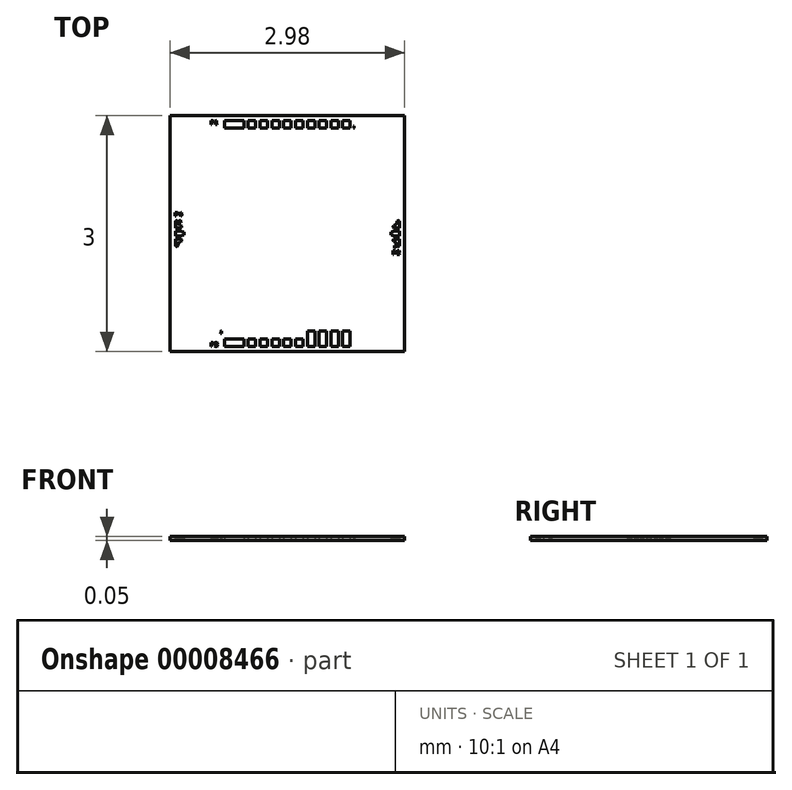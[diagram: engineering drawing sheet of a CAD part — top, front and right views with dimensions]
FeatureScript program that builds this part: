
annotation { "Feature Type Name" : "Feature", "Feature Type Description" : "" }
export const myFeature = defineFeature(function(context is Context, id is Id, definition is map)
    precondition{}
    {
        {
            var Q0;
            Q0=qCreatedBy(makeId("Top.planeOp"),FACE);
            var sketch = newSketch(context, id + "F0", { "sketchPlane" : qUnion([Q0])});
            skLineSegment(sketch, "E0", {"start": v(-1.43, 0.22) * mm, "end": v(-1.43, 0.27) * mm});
            skLineSegment(sketch, "E1", {"start": v(-1.43, 0.27) * mm, "end": v(-1.4, 0.27) * mm});
            skLineSegment(sketch, "E2", {"start": v(-1.4, 0.27) * mm, "end": v(-1.39, 0.26) * mm});
            skLineSegment(sketch, "E3", {"start": v(-1.39, 0.26) * mm, "end": v(-1.39, 0.25) * mm});
            skLineSegment(sketch, "E4", {"start": v(-1.39, 0.25) * mm, "end": v(-1.4, 0.24) * mm});
            skLineSegment(sketch, "E5", {"start": v(-1.4, 0.24) * mm, "end": v(-1.42, 0.24) * mm});
            skLineSegment(sketch, "E6", {"start": v(-1.42, 0.24) * mm, "end": v(-1.42, 0.22) * mm});
            skLineSegment(sketch, "E7", {"start": v(-1.42, 0.22) * mm, "end": v(-1.43, 0.22) * mm});
            skLineSegment(sketch, "E8", {"start": v(-1.42, -0.15) * mm, "end": v(-1.42, -0.07) * mm});
            skLineSegment(sketch, "E9", {"start": v(-1.42, -0.07) * mm, "end": v(-1.36, -0.07) * mm});
            skLineSegment(sketch, "E10", {"start": v(-1.36, -0.07) * mm, "end": v(-1.35, -0.07) * mm});
            skLineSegment(sketch, "E11", {"start": v(-1.35, -0.07) * mm, "end": v(-1.35, -0.07) * mm});
            skLineSegment(sketch, "E12", {"start": v(-1.35, -0.07) * mm, "end": v(-1.35, -0.08) * mm});
            skLineSegment(sketch, "E13", {"start": v(-1.35, -0.08) * mm, "end": v(-1.34, -0.08) * mm});
            skLineSegment(sketch, "E14", {"start": v(-1.34, -0.08) * mm, "end": v(-1.34, -0.09) * mm});
            skLineSegment(sketch, "E15", {"start": v(-1.34, -0.09) * mm, "end": v(-1.34, -0.1) * mm});
            skLineSegment(sketch, "E16", {"start": v(-1.34, -0.1) * mm, "end": v(-1.35, -0.1) * mm});
            skLineSegment(sketch, "E17", {"start": v(-1.35, -0.1) * mm, "end": v(-1.35, -0.1) * mm});
            skLineSegment(sketch, "E18", {"start": v(-1.35, -0.1) * mm, "end": v(-1.36, -0.1) * mm});
            skLineSegment(sketch, "E19", {"start": v(-1.36, -0.1) * mm, "end": v(-1.37, -0.1) * mm});
            skLineSegment(sketch, "E20", {"start": v(-1.37, -0.1) * mm, "end": v(-1.4, -0.14) * mm});
            skLineSegment(sketch, "E21", {"start": v(-1.4, -0.14) * mm, "end": v(-1.4, -0.15) * mm});
            skLineSegment(sketch, "E22", {"start": v(-1.4, -0.15) * mm, "end": v(-1.4, -0.15) * mm});
            skLineSegment(sketch, "E23", {"start": v(-1.4, -0.15) * mm, "end": v(-1.4, -0.16) * mm});
            skLineSegment(sketch, "E24", {"start": v(-1.4, -0.16) * mm, "end": v(-1.4, -0.16) * mm});
            skLineSegment(sketch, "E25", {"start": v(-1.4, -0.16) * mm, "end": v(-1.41, -0.16) * mm});
            skLineSegment(sketch, "E26", {"start": v(-1.41, -0.16) * mm, "end": v(-1.42, -0.16) * mm});
            skLineSegment(sketch, "E27", {"start": v(-1.42, -0.16) * mm, "end": v(-1.42, -0.16) * mm});
            skLineSegment(sketch, "E28", {"start": v(-1.42, -0.16) * mm, "end": v(-1.42, -0.15) * mm});
            skLineSegment(sketch, "E29", {"start": v(-1.42, -0.15) * mm, "end": v(-1.42, -0.15) * mm});
            skLineSegment(sketch, "E30", {"start": v(-1.42, -0.03) * mm, "end": v(-1.42, 0.03) * mm});
            skLineSegment(sketch, "E31", {"start": v(-1.42, 0.03) * mm, "end": v(-1.36, 0.03) * mm});
            skLineSegment(sketch, "E32", {"start": v(-1.36, 0.03) * mm, "end": v(-1.33, 0.02) * mm});
            skLineSegment(sketch, "E33", {"start": v(-1.33, 0.02) * mm, "end": v(-1.32, 0.02) * mm});
            skLineSegment(sketch, "E34", {"start": v(-1.32, 0.02) * mm, "end": v(-1.32, -0.02) * mm});
            skLineSegment(sketch, "E35", {"start": v(-1.32, -0.02) * mm, "end": v(-1.33, -0.02) * mm});
            skLineSegment(sketch, "E36", {"start": v(-1.33, -0.02) * mm, "end": v(-1.36, -0.03) * mm});
            skLineSegment(sketch, "E37", {"start": v(-1.36, -0.03) * mm, "end": v(-1.42, -0.03) * mm});
            skLineSegment(sketch, "E38", {"start": v(-1.36, 0.15) * mm, "end": v(-1.35, 0.15) * mm});
            skLineSegment(sketch, "E39", {"start": v(-1.35, 0.15) * mm, "end": v(-1.35, 0.14) * mm});
            skLineSegment(sketch, "E40", {"start": v(-1.35, 0.14) * mm, "end": v(-1.36, 0.14) * mm});
            skLineSegment(sketch, "E41", {"start": v(-1.36, 0.14) * mm, "end": v(-1.36, 0.15) * mm});
            skLineSegment(sketch, "E42", {"start": v(-1.36, 0.15) * mm, "end": v(-1.36, 0.15) * mm});
            skLineSegment(sketch, "E43", {"start": v(-1.36, 0.15) * mm, "end": v(-1.36, 0.17) * mm});
            skLineSegment(sketch, "E44", {"start": v(-1.36, 0.17) * mm, "end": v(-1.36, 0.17) * mm});
            skLineSegment(sketch, "E45", {"start": v(-1.36, 0.17) * mm, "end": v(-1.36, 0.15) * mm});
            skLineSegment(sketch, "E46", {"start": v(-1.34, 0.1) * mm, "end": v(-1.34, 0.09) * mm});
            skLineSegment(sketch, "E47", {"start": v(-1.34, 0.09) * mm, "end": v(-1.34, 0.08) * mm});
            skLineSegment(sketch, "E48", {"start": v(-1.34, 0.08) * mm, "end": v(-1.35, 0.08) * mm});
            skLineSegment(sketch, "E49", {"start": v(-1.35, 0.08) * mm, "end": v(-1.35, 0.07) * mm});
            skLineSegment(sketch, "E50", {"start": v(-1.35, 0.07) * mm, "end": v(-1.35, 0.07) * mm});
            skLineSegment(sketch, "E51", {"start": v(-1.35, 0.07) * mm, "end": v(-1.36, 0.07) * mm});
            skLineSegment(sketch, "E52", {"start": v(-1.36, 0.07) * mm, "end": v(-1.42, 0.07) * mm});
            skLineSegment(sketch, "E53", {"start": v(-1.42, 0.07) * mm, "end": v(-1.42, 0.15) * mm});
            skLineSegment(sketch, "E54", {"start": v(-1.42, 0.15) * mm, "end": v(-1.42, 0.15) * mm});
            skLineSegment(sketch, "E55", {"start": v(-1.42, 0.15) * mm, "end": v(-1.42, 0.16) * mm});
            skLineSegment(sketch, "E56", {"start": v(-1.42, 0.16) * mm, "end": v(-1.42, 0.16) * mm});
            skLineSegment(sketch, "E57", {"start": v(-1.42, 0.16) * mm, "end": v(-1.41, 0.16) * mm});
            skLineSegment(sketch, "E58", {"start": v(-1.41, 0.16) * mm, "end": v(-1.4, 0.16) * mm});
            skLineSegment(sketch, "E59", {"start": v(-1.4, 0.16) * mm, "end": v(-1.4, 0.16) * mm});
            skLineSegment(sketch, "E60", {"start": v(-1.4, 0.16) * mm, "end": v(-1.4, 0.15) * mm});
            skLineSegment(sketch, "E61", {"start": v(-1.4, 0.15) * mm, "end": v(-1.4, 0.15) * mm});
            skLineSegment(sketch, "E62", {"start": v(-1.4, 0.15) * mm, "end": v(-1.4, 0.14) * mm});
            skLineSegment(sketch, "E63", {"start": v(-1.4, 0.14) * mm, "end": v(-1.37, 0.1) * mm});
            skLineSegment(sketch, "E64", {"start": v(-1.37, 0.1) * mm, "end": v(-1.36, 0.1) * mm});
            skLineSegment(sketch, "E65", {"start": v(-1.36, 0.1) * mm, "end": v(-1.35, 0.1) * mm});
            skLineSegment(sketch, "E66", {"start": v(-1.35, 0.1) * mm, "end": v(-1.35, 0.1) * mm});
            skLineSegment(sketch, "E67", {"start": v(-1.35, 0.1) * mm, "end": v(-1.34, 0.1) * mm});
            skLineSegment(sketch, "E68", {"start": v(-1.35, 0.24) * mm, "end": v(-1.34, 0.24) * mm});
            skLineSegment(sketch, "E69", {"start": v(-1.34, 0.24) * mm, "end": v(-1.34, 0.24) * mm});
            skLineSegment(sketch, "E70", {"start": v(-1.34, 0.24) * mm, "end": v(-1.35, 0.24) * mm});
            skLineSegment(sketch, "E71", {"start": v(-1.35, 0.24) * mm, "end": v(-1.35, 0.22) * mm});
            skLineSegment(sketch, "E72", {"start": v(-1.35, 0.22) * mm, "end": v(-1.35, 0.22) * mm});
            skLineSegment(sketch, "E73", {"start": v(-1.35, 0.22) * mm, "end": v(-1.35, 0.24) * mm});
            skLineSegment(sketch, "E74", {"start": v(-1.35, 0.24) * mm, "end": v(-1.38, 0.24) * mm});
            skLineSegment(sketch, "E75", {"start": v(-1.38, 0.24) * mm, "end": v(-1.38, 0.24) * mm});
            skLineSegment(sketch, "E76", {"start": v(-1.38, 0.24) * mm, "end": v(-1.35, 0.27) * mm});
            skLineSegment(sketch, "E77", {"start": v(-1.35, 0.27) * mm, "end": v(-1.35, 0.27) * mm});
            skLineSegment(sketch, "E78", {"start": v(-1.35, 0.27) * mm, "end": v(-1.35, 0.24) * mm});
            skLineSegment(sketch, "E79", {"start": v(-0.97, -1.44) * mm, "end": v(-0.97, -1.39) * mm});
            skLineSegment(sketch, "E80", {"start": v(-0.97, -1.39) * mm, "end": v(-0.94, -1.39) * mm});
            skLineSegment(sketch, "E81", {"start": v(-0.94, -1.39) * mm, "end": v(-0.94, -1.4) * mm});
            skLineSegment(sketch, "E82", {"start": v(-0.94, -1.4) * mm, "end": v(-0.94, -1.4) * mm});
            skLineSegment(sketch, "E83", {"start": v(-0.94, -1.4) * mm, "end": v(-0.94, -1.41) * mm});
            skLineSegment(sketch, "E84", {"start": v(-0.94, -1.41) * mm, "end": v(-0.97, -1.41) * mm});
            skLineSegment(sketch, "E85", {"start": v(-0.97, -1.41) * mm, "end": v(-0.97, -1.44) * mm});
            skLineSegment(sketch, "E86", {"start": v(-0.97, -1.44) * mm, "end": v(-0.97, -1.44) * mm});
            skLineSegment(sketch, "E87", {"start": v(-0.9, -1.39) * mm, "end": v(-0.89, -1.4) * mm});
            skLineSegment(sketch, "E88", {"start": v(-0.89, -1.4) * mm, "end": v(-0.89, -1.4) * mm});
            skLineSegment(sketch, "E89", {"start": v(-0.89, -1.4) * mm, "end": v(-0.9, -1.41) * mm});
            skLineSegment(sketch, "E90", {"start": v(-0.9, -1.41) * mm, "end": v(-0.89, -1.42) * mm});
            skLineSegment(sketch, "E91", {"start": v(-0.89, -1.42) * mm, "end": v(-0.89, -1.43) * mm});
            skLineSegment(sketch, "E92", {"start": v(-0.89, -1.43) * mm, "end": v(-0.9, -1.44) * mm});
            skLineSegment(sketch, "E93", {"start": v(-0.9, -1.44) * mm, "end": v(-0.92, -1.44) * mm});
            skLineSegment(sketch, "E94", {"start": v(-0.92, -1.44) * mm, "end": v(-0.92, -1.43) * mm});
            skLineSegment(sketch, "E95", {"start": v(-0.92, -1.43) * mm, "end": v(-0.92, -1.42) * mm});
            skLineSegment(sketch, "E96", {"start": v(-0.92, -1.42) * mm, "end": v(-0.91, -1.43) * mm});
            skLineSegment(sketch, "E97", {"start": v(-0.91, -1.43) * mm, "end": v(-0.9, -1.43) * mm});
            skLineSegment(sketch, "E98", {"start": v(-0.9, -1.43) * mm, "end": v(-0.9, -1.42) * mm});
            skLineSegment(sketch, "E99", {"start": v(-0.9, -1.42) * mm, "end": v(-0.9, -1.42) * mm});
            skLineSegment(sketch, "E100", {"start": v(-0.9, -1.42) * mm, "end": v(-0.9, -1.41) * mm});
            skLineSegment(sketch, "E101", {"start": v(-0.9, -1.41) * mm, "end": v(-0.9, -1.41) * mm});
            skLineSegment(sketch, "E102", {"start": v(-0.9, -1.41) * mm, "end": v(-0.9, -1.4) * mm});
            skLineSegment(sketch, "E103", {"start": v(-0.9, -1.4) * mm, "end": v(-0.9, -1.4) * mm});
            skLineSegment(sketch, "E104", {"start": v(-0.9, -1.4) * mm, "end": v(-0.91, -1.4) * mm});
            skLineSegment(sketch, "E105", {"start": v(-0.91, -1.4) * mm, "end": v(-0.92, -1.4) * mm});
            skLineSegment(sketch, "E106", {"start": v(-0.92, -1.4) * mm, "end": v(-0.92, -1.4) * mm});
            skLineSegment(sketch, "E107", {"start": v(-0.92, -1.4) * mm, "end": v(-0.92, -1.39) * mm});
            skLineSegment(sketch, "E108", {"start": v(-0.92, -1.39) * mm, "end": v(-0.9, -1.39) * mm});
            skLineSegment(sketch, "E109", {"start": v(-0.84, -1.26) * mm, "end": v(-0.83, -1.26) * mm});
            skLineSegment(sketch, "E110", {"start": v(-0.83, -1.26) * mm, "end": v(-0.83, -1.27) * mm});
            skLineSegment(sketch, "E111", {"start": v(-0.83, -1.27) * mm, "end": v(-0.85, -1.27) * mm});
            skLineSegment(sketch, "E112", {"start": v(-0.85, -1.27) * mm, "end": v(-0.85, -1.26) * mm});
            skLineSegment(sketch, "E113", {"start": v(-0.85, -1.26) * mm, "end": v(-0.84, -1.26) * mm});
            skLineSegment(sketch, "E114", {"start": v(-0.84, -1.26) * mm, "end": v(-0.84, -1.24) * mm});
            skLineSegment(sketch, "E115", {"start": v(-0.84, -1.24) * mm, "end": v(-0.85, -1.24) * mm});
            skLineSegment(sketch, "E116", {"start": v(-0.85, -1.24) * mm, "end": v(-0.84, -1.24) * mm});
            skLineSegment(sketch, "E117", {"start": v(-0.84, -1.24) * mm, "end": v(-0.84, -1.24) * mm});
            skLineSegment(sketch, "E118", {"start": v(-0.84, -1.24) * mm, "end": v(-0.84, -1.26) * mm});
            skLineSegment(sketch, "E119", {"start": v(-0.8, -1.43) * mm, "end": v(-0.8, -1.34) * mm});
            skLineSegment(sketch, "E120", {"start": v(-0.8, -1.34) * mm, "end": v(-0.55, -1.34) * mm});
            skLineSegment(sketch, "E121", {"start": v(-0.55, -1.34) * mm, "end": v(-0.55, -1.43) * mm});
            skLineSegment(sketch, "E122", {"start": v(-0.55, -1.43) * mm, "end": v(-0.8, -1.43) * mm});
            skLineSegment(sketch, "E123", {"start": v(-0.8, 1.34) * mm, "end": v(-0.8, 1.43) * mm});
            skLineSegment(sketch, "E124", {"start": v(-0.8, 1.43) * mm, "end": v(-0.55, 1.43) * mm});
            skLineSegment(sketch, "E125", {"start": v(-0.55, 1.43) * mm, "end": v(-0.55, 1.34) * mm});
            skLineSegment(sketch, "E126", {"start": v(-0.55, 1.34) * mm, "end": v(-0.8, 1.34) * mm});
            skLineSegment(sketch, "E127", {"start": v(-0.5, -1.43) * mm, "end": v(-0.5, -1.34) * mm});
            skLineSegment(sketch, "E128", {"start": v(-0.5, -1.34) * mm, "end": v(-0.4, -1.34) * mm});
            skLineSegment(sketch, "E129", {"start": v(-0.4, -1.34) * mm, "end": v(-0.4, -1.43) * mm});
            skLineSegment(sketch, "E130", {"start": v(-0.4, -1.43) * mm, "end": v(-0.5, -1.43) * mm});
            skLineSegment(sketch, "E131", {"start": v(-0.5, 1.34) * mm, "end": v(-0.5, 1.43) * mm});
            skLineSegment(sketch, "E132", {"start": v(-0.5, 1.43) * mm, "end": v(-0.4, 1.43) * mm});
            skLineSegment(sketch, "E133", {"start": v(-0.4, 1.43) * mm, "end": v(-0.4, 1.34) * mm});
            skLineSegment(sketch, "E134", {"start": v(-0.4, 1.34) * mm, "end": v(-0.5, 1.34) * mm});
            skLineSegment(sketch, "E135", {"start": v(-0.35, -1.43) * mm, "end": v(-0.35, -1.34) * mm});
            skLineSegment(sketch, "E136", {"start": v(-0.35, -1.34) * mm, "end": v(-0.25, -1.34) * mm});
            skLineSegment(sketch, "E137", {"start": v(-0.25, -1.34) * mm, "end": v(-0.25, -1.43) * mm});
            skLineSegment(sketch, "E138", {"start": v(-0.25, -1.43) * mm, "end": v(-0.35, -1.43) * mm});
            skLineSegment(sketch, "E139", {"start": v(-0.35, 1.34) * mm, "end": v(-0.35, 1.43) * mm});
            skLineSegment(sketch, "E140", {"start": v(-0.35, 1.43) * mm, "end": v(-0.25, 1.43) * mm});
            skLineSegment(sketch, "E141", {"start": v(-0.25, 1.43) * mm, "end": v(-0.25, 1.34) * mm});
            skLineSegment(sketch, "E142", {"start": v(-0.25, 1.34) * mm, "end": v(-0.35, 1.34) * mm});
            skLineSegment(sketch, "E143", {"start": v(-0.2, -1.43) * mm, "end": v(-0.2, -1.34) * mm});
            skLineSegment(sketch, "E144", {"start": v(-0.2, -1.34) * mm, "end": v(-0.1, -1.34) * mm});
            skLineSegment(sketch, "E145", {"start": v(-0.1, -1.34) * mm, "end": v(-0.1, -1.43) * mm});
            skLineSegment(sketch, "E146", {"start": v(-0.1, -1.43) * mm, "end": v(-0.2, -1.43) * mm});
            skLineSegment(sketch, "E147", {"start": v(-0.2, 1.34) * mm, "end": v(-0.2, 1.43) * mm});
            skLineSegment(sketch, "E148", {"start": v(-0.2, 1.43) * mm, "end": v(-0.1, 1.43) * mm});
            skLineSegment(sketch, "E149", {"start": v(-0.1, 1.43) * mm, "end": v(-0.1, 1.34) * mm});
            skLineSegment(sketch, "E150", {"start": v(-0.1, 1.34) * mm, "end": v(-0.2, 1.34) * mm});
            skLineSegment(sketch, "E151", {"start": v(-0.05, -1.43) * mm, "end": v(-0.05, -1.34) * mm});
            skLineSegment(sketch, "E152", {"start": v(-0.05, -1.34) * mm, "end": v(0.05, -1.34) * mm});
            skLineSegment(sketch, "E153", {"start": v(0.05, -1.34) * mm, "end": v(0.05, -1.43) * mm});
            skLineSegment(sketch, "E154", {"start": v(0.05, -1.43) * mm, "end": v(-0.05, -1.43) * mm});
            skLineSegment(sketch, "E155", {"start": v(-0.05, 1.34) * mm, "end": v(-0.05, 1.43) * mm});
            skLineSegment(sketch, "E156", {"start": v(-0.05, 1.43) * mm, "end": v(0.05, 1.43) * mm});
            skLineSegment(sketch, "E157", {"start": v(0.05, 1.43) * mm, "end": v(0.05, 1.34) * mm});
            skLineSegment(sketch, "E158", {"start": v(0.05, 1.34) * mm, "end": v(-0.05, 1.34) * mm});
            skLineSegment(sketch, "E159", {"start": v(0.1, -1.43) * mm, "end": v(0.1, -1.34) * mm});
            skLineSegment(sketch, "E160", {"start": v(0.1, -1.34) * mm, "end": v(0.2, -1.34) * mm});
            skLineSegment(sketch, "E161", {"start": v(0.2, -1.34) * mm, "end": v(0.2, -1.43) * mm});
            skLineSegment(sketch, "E162", {"start": v(0.2, -1.43) * mm, "end": v(0.1, -1.43) * mm});
            skLineSegment(sketch, "E163", {"start": v(0.1, 1.34) * mm, "end": v(0.1, 1.43) * mm});
            skLineSegment(sketch, "E164", {"start": v(0.1, 1.43) * mm, "end": v(0.2, 1.43) * mm});
            skLineSegment(sketch, "E165", {"start": v(0.2, 1.43) * mm, "end": v(0.2, 1.34) * mm});
            skLineSegment(sketch, "E166", {"start": v(0.2, 1.34) * mm, "end": v(0.1, 1.34) * mm});
            skLineSegment(sketch, "E167", {"start": v(0.25, -1.43) * mm, "end": v(0.25, -1.24) * mm});
            skLineSegment(sketch, "E168", {"start": v(0.25, -1.24) * mm, "end": v(0.35, -1.24) * mm});
            skLineSegment(sketch, "E169", {"start": v(0.35, -1.24) * mm, "end": v(0.35, -1.43) * mm});
            skLineSegment(sketch, "E170", {"start": v(0.35, -1.43) * mm, "end": v(0.25, -1.43) * mm});
            skLineSegment(sketch, "E171", {"start": v(0.4, -1.43) * mm, "end": v(0.4, -1.24) * mm});
            skLineSegment(sketch, "E172", {"start": v(0.4, -1.24) * mm, "end": v(0.5, -1.24) * mm});
            skLineSegment(sketch, "E173", {"start": v(0.5, -1.24) * mm, "end": v(0.5, -1.43) * mm});
            skLineSegment(sketch, "E174", {"start": v(0.5, -1.43) * mm, "end": v(0.4, -1.43) * mm});
            skLineSegment(sketch, "E175", {"start": v(0.55, -1.43) * mm, "end": v(0.55, -1.24) * mm});
            skLineSegment(sketch, "E176", {"start": v(0.55, -1.24) * mm, "end": v(0.65, -1.24) * mm});
            skLineSegment(sketch, "E177", {"start": v(0.65, -1.24) * mm, "end": v(0.65, -1.43) * mm});
            skLineSegment(sketch, "E178", {"start": v(0.65, -1.43) * mm, "end": v(0.55, -1.43) * mm});
            skLineSegment(sketch, "E179", {"start": v(0.7, -1.43) * mm, "end": v(0.7, -1.24) * mm});
            skLineSegment(sketch, "E180", {"start": v(0.7, -1.24) * mm, "end": v(0.8, -1.24) * mm});
            skLineSegment(sketch, "E181", {"start": v(0.8, -1.24) * mm, "end": v(0.8, -1.43) * mm});
            skLineSegment(sketch, "E182", {"start": v(0.8, -1.43) * mm, "end": v(0.7, -1.43) * mm});
            skLineSegment(sketch, "E183", {"start": v(1.32, -0.02) * mm, "end": v(1.32, 0.02) * mm});
            skLineSegment(sketch, "E184", {"start": v(1.32, 0.02) * mm, "end": v(1.33, 0.02) * mm});
            skLineSegment(sketch, "E185", {"start": v(1.33, 0.02) * mm, "end": v(1.36, 0.03) * mm});
            skLineSegment(sketch, "E186", {"start": v(1.36, 0.03) * mm, "end": v(1.42, 0.03) * mm});
            skLineSegment(sketch, "E187", {"start": v(1.42, 0.03) * mm, "end": v(1.42, -0.03) * mm});
            skLineSegment(sketch, "E188", {"start": v(1.42, -0.03) * mm, "end": v(1.36, -0.03) * mm});
            skLineSegment(sketch, "E189", {"start": v(1.36, -0.03) * mm, "end": v(1.33, -0.02) * mm});
            skLineSegment(sketch, "E190", {"start": v(1.33, -0.02) * mm, "end": v(1.32, -0.02) * mm});
            skLineSegment(sketch, "E191", {"start": v(1.34, -0.27) * mm, "end": v(1.34, -0.22) * mm});
            skLineSegment(sketch, "E192", {"start": v(1.34, -0.22) * mm, "end": v(1.37, -0.22) * mm});
            skLineSegment(sketch, "E193", {"start": v(1.37, -0.22) * mm, "end": v(1.38, -0.23) * mm});
            skLineSegment(sketch, "E194", {"start": v(1.38, -0.23) * mm, "end": v(1.38, -0.24) * mm});
            skLineSegment(sketch, "E195", {"start": v(1.38, -0.24) * mm, "end": v(1.37, -0.25) * mm});
            skLineSegment(sketch, "E196", {"start": v(1.37, -0.25) * mm, "end": v(1.35, -0.25) * mm});
            skLineSegment(sketch, "E197", {"start": v(1.35, -0.25) * mm, "end": v(1.35, -0.27) * mm});
            skLineSegment(sketch, "E198", {"start": v(1.35, -0.27) * mm, "end": v(1.34, -0.27) * mm});
            skLineSegment(sketch, "E199", {"start": v(1.37, -0.18) * mm, "end": v(1.37, -0.18) * mm});
            skLineSegment(sketch, "E200", {"start": v(1.37, -0.18) * mm, "end": v(1.36, -0.18) * mm});
            skLineSegment(sketch, "E201", {"start": v(1.36, -0.18) * mm, "end": v(1.36, -0.18) * mm});
            skLineSegment(sketch, "E202", {"start": v(1.36, -0.18) * mm, "end": v(1.36, -0.16) * mm});
            skLineSegment(sketch, "E203", {"start": v(1.36, -0.16) * mm, "end": v(1.36, -0.16) * mm});
            skLineSegment(sketch, "E204", {"start": v(1.36, -0.16) * mm, "end": v(1.36, -0.15) * mm});
            skLineSegment(sketch, "E205", {"start": v(1.36, -0.15) * mm, "end": v(1.37, -0.15) * mm});
            skLineSegment(sketch, "E206", {"start": v(1.37, -0.15) * mm, "end": v(1.37, -0.18) * mm});
            skLineSegment(sketch, "E207", {"start": v(1.39, -0.27) * mm, "end": v(1.39, -0.26) * mm});
            skLineSegment(sketch, "E208", {"start": v(1.39, -0.26) * mm, "end": v(1.42, -0.24) * mm});
            skLineSegment(sketch, "E209", {"start": v(1.42, -0.24) * mm, "end": v(1.42, -0.23) * mm});
            skLineSegment(sketch, "E210", {"start": v(1.42, -0.23) * mm, "end": v(1.41, -0.23) * mm});
            skLineSegment(sketch, "E211", {"start": v(1.41, -0.23) * mm, "end": v(1.4, -0.23) * mm});
            skLineSegment(sketch, "E212", {"start": v(1.4, -0.23) * mm, "end": v(1.4, -0.23) * mm});
            skLineSegment(sketch, "E213", {"start": v(1.4, -0.23) * mm, "end": v(1.39, -0.23) * mm});
            skLineSegment(sketch, "E214", {"start": v(1.39, -0.23) * mm, "end": v(1.4, -0.22) * mm});
            skLineSegment(sketch, "E215", {"start": v(1.4, -0.22) * mm, "end": v(1.42, -0.22) * mm});
            skLineSegment(sketch, "E216", {"start": v(1.42, -0.22) * mm, "end": v(1.43, -0.23) * mm});
            skLineSegment(sketch, "E217", {"start": v(1.43, -0.23) * mm, "end": v(1.43, -0.24) * mm});
            skLineSegment(sketch, "E218", {"start": v(1.43, -0.24) * mm, "end": v(1.4, -0.26) * mm});
            skLineSegment(sketch, "E219", {"start": v(1.4, -0.26) * mm, "end": v(1.43, -0.26) * mm});
            skLineSegment(sketch, "E220", {"start": v(1.43, -0.26) * mm, "end": v(1.43, -0.27) * mm});
            skLineSegment(sketch, "E221", {"start": v(1.43, -0.27) * mm, "end": v(1.39, -0.27) * mm});
            skLineSegment(sketch, "E222", {"start": v(1.4, -0.15) * mm, "end": v(1.4, -0.14) * mm});
            skLineSegment(sketch, "E223", {"start": v(1.4, -0.14) * mm, "end": v(1.37, -0.1) * mm});
            skLineSegment(sketch, "E224", {"start": v(1.37, -0.1) * mm, "end": v(1.36, -0.1) * mm});
            skLineSegment(sketch, "E225", {"start": v(1.36, -0.1) * mm, "end": v(1.35, -0.1) * mm});
            skLineSegment(sketch, "E226", {"start": v(1.35, -0.1) * mm, "end": v(1.35, -0.1) * mm});
            skLineSegment(sketch, "E227", {"start": v(1.35, -0.1) * mm, "end": v(1.34, -0.1) * mm});
            skLineSegment(sketch, "E228", {"start": v(1.34, -0.1) * mm, "end": v(1.34, -0.09) * mm});
            skLineSegment(sketch, "E229", {"start": v(1.34, -0.09) * mm, "end": v(1.34, -0.08) * mm});
            skLineSegment(sketch, "E230", {"start": v(1.34, -0.08) * mm, "end": v(1.35, -0.08) * mm});
            skLineSegment(sketch, "E231", {"start": v(1.35, -0.08) * mm, "end": v(1.35, -0.07) * mm});
            skLineSegment(sketch, "E232", {"start": v(1.35, -0.07) * mm, "end": v(1.35, -0.07) * mm});
            skLineSegment(sketch, "E233", {"start": v(1.35, -0.07) * mm, "end": v(1.36, -0.07) * mm});
            skLineSegment(sketch, "E234", {"start": v(1.36, -0.07) * mm, "end": v(1.42, -0.07) * mm});
            skLineSegment(sketch, "E235", {"start": v(1.42, -0.07) * mm, "end": v(1.42, -0.15) * mm});
            skLineSegment(sketch, "E236", {"start": v(1.42, -0.15) * mm, "end": v(1.42, -0.15) * mm});
            skLineSegment(sketch, "E237", {"start": v(1.42, -0.15) * mm, "end": v(1.42, -0.16) * mm});
            skLineSegment(sketch, "E238", {"start": v(1.42, -0.16) * mm, "end": v(1.42, -0.16) * mm});
            skLineSegment(sketch, "E239", {"start": v(1.42, -0.16) * mm, "end": v(1.41, -0.16) * mm});
            skLineSegment(sketch, "E240", {"start": v(1.41, -0.16) * mm, "end": v(1.4, -0.16) * mm});
            skLineSegment(sketch, "E241", {"start": v(1.4, -0.16) * mm, "end": v(1.4, -0.16) * mm});
            skLineSegment(sketch, "E242", {"start": v(1.4, -0.16) * mm, "end": v(1.4, -0.15) * mm});
            skLineSegment(sketch, "E243", {"start": v(1.4, -0.15) * mm, "end": v(1.4, -0.15) * mm});
            skLineSegment(sketch, "E244", {"start": v(1.42, 0.15) * mm, "end": v(1.42, 0.15) * mm});
            skLineSegment(sketch, "E245", {"start": v(1.42, 0.15) * mm, "end": v(1.42, 0.07) * mm});
            skLineSegment(sketch, "E246", {"start": v(1.42, 0.07) * mm, "end": v(1.36, 0.07) * mm});
            skLineSegment(sketch, "E247", {"start": v(1.36, 0.07) * mm, "end": v(1.35, 0.07) * mm});
            skLineSegment(sketch, "E248", {"start": v(1.35, 0.07) * mm, "end": v(1.35, 0.07) * mm});
            skLineSegment(sketch, "E249", {"start": v(1.35, 0.07) * mm, "end": v(1.35, 0.08) * mm});
            skLineSegment(sketch, "E250", {"start": v(1.35, 0.08) * mm, "end": v(1.34, 0.08) * mm});
            skLineSegment(sketch, "E251", {"start": v(1.34, 0.08) * mm, "end": v(1.34, 0.09) * mm});
            skLineSegment(sketch, "E252", {"start": v(1.34, 0.09) * mm, "end": v(1.34, 0.1) * mm});
            skLineSegment(sketch, "E253", {"start": v(1.34, 0.1) * mm, "end": v(1.35, 0.1) * mm});
            skLineSegment(sketch, "E254", {"start": v(1.35, 0.1) * mm, "end": v(1.35, 0.1) * mm});
            skLineSegment(sketch, "E255", {"start": v(1.35, 0.1) * mm, "end": v(1.36, 0.1) * mm});
            skLineSegment(sketch, "E256", {"start": v(1.36, 0.1) * mm, "end": v(1.37, 0.1) * mm});
            skLineSegment(sketch, "E257", {"start": v(1.37, 0.1) * mm, "end": v(1.4, 0.14) * mm});
            skLineSegment(sketch, "E258", {"start": v(1.4, 0.14) * mm, "end": v(1.4, 0.15) * mm});
            skLineSegment(sketch, "E259", {"start": v(1.4, 0.15) * mm, "end": v(1.4, 0.15) * mm});
            skLineSegment(sketch, "E260", {"start": v(1.4, 0.15) * mm, "end": v(1.4, 0.16) * mm});
            skLineSegment(sketch, "E261", {"start": v(1.4, 0.16) * mm, "end": v(1.4, 0.16) * mm});
            skLineSegment(sketch, "E262", {"start": v(1.4, 0.16) * mm, "end": v(1.41, 0.16) * mm});
            skLineSegment(sketch, "E263", {"start": v(1.41, 0.16) * mm, "end": v(1.42, 0.16) * mm});
            skLineSegment(sketch, "E264", {"start": v(1.42, 0.16) * mm, "end": v(1.42, 0.16) * mm});
            skLineSegment(sketch, "E265", {"start": v(1.42, 0.16) * mm, "end": v(1.42, 0.15) * mm});
            skLineSegment(sketch, "E266", {"start": v(-0.97, 1.39) * mm, "end": v(-0.97, 1.44) * mm});
            skLineSegment(sketch, "E267", {"start": v(-0.97, 1.44) * mm, "end": v(-0.94, 1.44) * mm});
            skLineSegment(sketch, "E268", {"start": v(-0.94, 1.44) * mm, "end": v(-0.94, 1.43) * mm});
            skLineSegment(sketch, "E269", {"start": v(-0.94, 1.43) * mm, "end": v(-0.94, 1.41) * mm});
            skLineSegment(sketch, "E270", {"start": v(-0.94, 1.41) * mm, "end": v(-0.94, 1.4) * mm});
            skLineSegment(sketch, "E271", {"start": v(-0.94, 1.4) * mm, "end": v(-0.97, 1.4) * mm});
            skLineSegment(sketch, "E272", {"start": v(-0.97, 1.4) * mm, "end": v(-0.97, 1.39) * mm});
            skLineSegment(sketch, "E273", {"start": v(-0.97, 1.39) * mm, "end": v(-0.97, 1.39) * mm});
            skLineSegment(sketch, "E274", {"start": v(-0.9, 1.4) * mm, "end": v(-0.9, 1.4) * mm});
            skLineSegment(sketch, "E275", {"start": v(-0.9, 1.4) * mm, "end": v(-0.9, 1.39) * mm});
            skLineSegment(sketch, "E276", {"start": v(-0.9, 1.39) * mm, "end": v(-0.92, 1.39) * mm});
            skLineSegment(sketch, "E277", {"start": v(-0.92, 1.39) * mm, "end": v(-0.92, 1.4) * mm});
            skLineSegment(sketch, "E278", {"start": v(-0.92, 1.4) * mm, "end": v(-0.9, 1.4) * mm});
            skLineSegment(sketch, "E279", {"start": v(-0.9, 1.4) * mm, "end": v(-0.9, 1.43) * mm});
            skLineSegment(sketch, "E280", {"start": v(-0.9, 1.43) * mm, "end": v(-0.92, 1.43) * mm});
            skLineSegment(sketch, "E281", {"start": v(-0.92, 1.43) * mm, "end": v(-0.9, 1.44) * mm});
            skLineSegment(sketch, "E282", {"start": v(-0.9, 1.44) * mm, "end": v(-0.9, 1.44) * mm});
            skLineSegment(sketch, "E283", {"start": v(-0.9, 1.44) * mm, "end": v(-0.9, 1.4) * mm});
            skLineSegment(sketch, "E284", {"start": v(0.25, 1.34) * mm, "end": v(0.35, 1.34) * mm});
            skLineSegment(sketch, "E285", {"start": v(0.35, 1.34) * mm, "end": v(0.35, 1.43) * mm});
            skLineSegment(sketch, "E286", {"start": v(0.35, 1.43) * mm, "end": v(0.25, 1.43) * mm});
            skLineSegment(sketch, "E287", {"start": v(0.25, 1.43) * mm, "end": v(0.25, 1.34) * mm});
            skLineSegment(sketch, "E288", {"start": v(0.4, 1.34) * mm, "end": v(0.5, 1.34) * mm});
            skLineSegment(sketch, "E289", {"start": v(0.5, 1.34) * mm, "end": v(0.5, 1.43) * mm});
            skLineSegment(sketch, "E290", {"start": v(0.5, 1.43) * mm, "end": v(0.4, 1.43) * mm});
            skLineSegment(sketch, "E291", {"start": v(0.4, 1.43) * mm, "end": v(0.4, 1.34) * mm});
            skLineSegment(sketch, "E292", {"start": v(0.55, 1.34) * mm, "end": v(0.65, 1.34) * mm});
            skLineSegment(sketch, "E293", {"start": v(0.65, 1.34) * mm, "end": v(0.65, 1.43) * mm});
            skLineSegment(sketch, "E294", {"start": v(0.65, 1.43) * mm, "end": v(0.55, 1.43) * mm});
            skLineSegment(sketch, "E295", {"start": v(0.55, 1.43) * mm, "end": v(0.55, 1.34) * mm});
            skLineSegment(sketch, "E296", {"start": v(0.7, 1.34) * mm, "end": v(0.8, 1.34) * mm});
            skLineSegment(sketch, "E297", {"start": v(0.8, 1.34) * mm, "end": v(0.8, 1.43) * mm});
            skLineSegment(sketch, "E298", {"start": v(0.8, 1.43) * mm, "end": v(0.7, 1.43) * mm});
            skLineSegment(sketch, "E299", {"start": v(0.7, 1.43) * mm, "end": v(0.7, 1.34) * mm});
            skLineSegment(sketch, "E300", {"start": v(0.85, 1.34) * mm, "end": v(0.85, 1.34) * mm});
            skLineSegment(sketch, "E301", {"start": v(0.85, 1.34) * mm, "end": v(0.84, 1.34) * mm});
            skLineSegment(sketch, "E302", {"start": v(0.84, 1.34) * mm, "end": v(0.84, 1.34) * mm});
            skLineSegment(sketch, "E303", {"start": v(0.84, 1.34) * mm, "end": v(0.84, 1.36) * mm});
            skLineSegment(sketch, "E304", {"start": v(0.84, 1.36) * mm, "end": v(0.84, 1.36) * mm});
            skLineSegment(sketch, "E305", {"start": v(0.84, 1.36) * mm, "end": v(0.84, 1.37) * mm});
            skLineSegment(sketch, "E306", {"start": v(0.84, 1.37) * mm, "end": v(0.85, 1.37) * mm});
            skLineSegment(sketch, "E307", {"start": v(0.85, 1.37) * mm, "end": v(0.85, 1.34) * mm});
            skSolve(sketch);
        }
        {
            var Q0;
            Q0 = qSketchRegion(id + "F0", true);
            extrude(context, id + "F1", {"entities" : qUnion([Q0]), "depth" : 0.05 * mm});
        }
        {
            var Q0;
            Q0=qCreatedBy(makeId("Top.planeOp"),FACE);
            var sketch = newSketch(context, id + "F2", { "sketchPlane" : qUnion([Q0])});
            skLineSegment(sketch, "E308.bottom", {"start": v(-1.5, 1.5) * mm, "end": v(1.5, 1.5) * mm});
            skLineSegment(sketch, "E308.top", {"start": v(-1.5, -1.5) * mm, "end": v(1.5, -1.5) * mm});
            skLineSegment(sketch, "E308.left", {"start": v(-1.49, 1.5) * mm, "end": v(-1.5, -1.5) * mm});
            skLineSegment(sketch, "E308.right", {"start": v(1.5, 1.5) * mm, "end": v(1.49, -1.5) * mm});
            skSolve(sketch);
        }
        {
            var Q0;
            Q0 = qSketchRegion(id + "F2", true);
            extrude(context, id + "F3", {"entities" : qUnion([Q0]), "depth" : 0.05 * mm});
        }
    });
